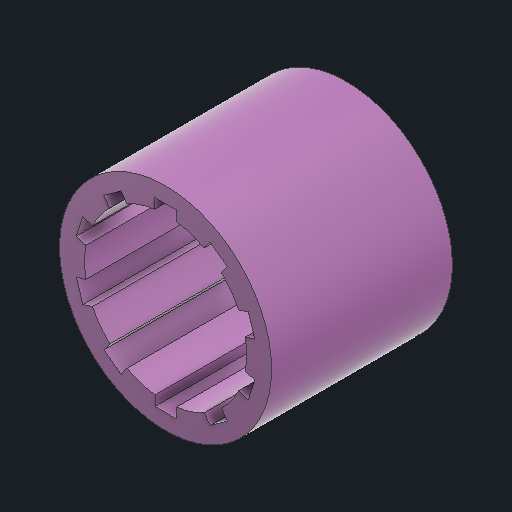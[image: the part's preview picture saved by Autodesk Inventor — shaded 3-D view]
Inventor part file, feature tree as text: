
AUTODESK INVENTOR PART (.ipt)
format: ipt  version: 2024 (Build 280153000, 153)  size: 196,096 bytes
history: native  units: in
note: dims shown in document units (in); Inventor stores cm internally (conversion verified against a paired STEP export)
features: extrude x1, sketch x1
ambient origin geometry x8: Origin, YZ Plane, XZ Plane, XY Plane, X Axis, Y Axis, Z Axis, Center Point
bodies: Solid1 (feature_tree)
feature tree (2):
  extrude  "Extrusion1"  Depth=1.1417in
  sketch  "Sketch1"  dims[d1=3.937in d2=360.0deg d3=1.3386in d4=1.1417in d5=0.0in]
